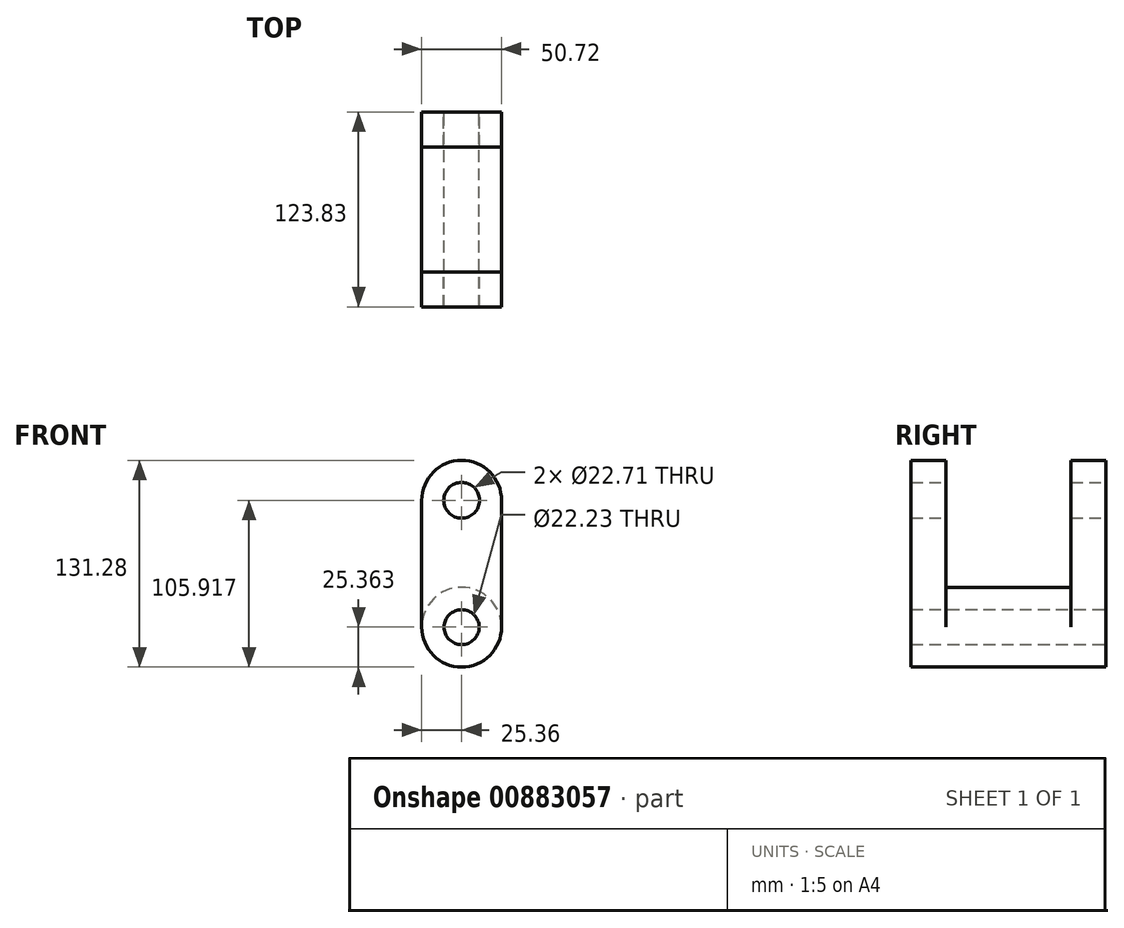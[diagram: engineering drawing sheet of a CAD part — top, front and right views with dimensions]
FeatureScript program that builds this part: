
annotation { "Feature Type Name" : "Feature", "Feature Type Description" : "" }
export const myFeature = defineFeature(function(context is Context, id is Id, definition is map)
    precondition{}
    {
        {
            var Q0;
            Q0=qCreatedBy(makeId("Front.planeOp"),FACE);
            var sketch = newSketch(context, id + "F0", { "sketchPlane" : qUnion([Q0])});
            skLineSegment(sketch, "E0.left", {"start": v(25.36, 40.28) * mm, "end": v(25.36, -40.28) * mm});
            skLineSegment(sketch, "E0.right", {"start": v(-25.36, 40.28) * mm, "end": v(-25.36, -40.28) * mm});
            skPoint(sketch, "E0.middle", {"position": v(0, 0) * mm});
            skArc(sketch, "E1", {"start": v(25.36, 40.28) * mm, "mid": v(0, 65.64) * mm, "end": v(-25.36, 40.28) * mm});
            skArc(sketch, "E2", {"start": v(-25.36, -40.28) * mm, "mid": v(0, -65.64) * mm, "end": v(25.36, -40.28) * mm});
            skCircle(sketch, "E3", {"center": v(0, 40.28) * mm, "radius": 11.35 * mm});
            skSolve(sketch);
        }
        {
            var Q0;
            Q0=makeQuery(id+"F0.imprint","IMPRINT",FACE,{"disambiguationData":[TD([[makeQuery(id+"F0.imprint","IMPRINT",EDGE,{"derivedFrom":sQuery(id+"F0.wireOp",EDGE,"E0.left")}),-1.0]])]});
            extrude(context, id + "F1", {"entities" : qUnion([Q0]), "depth" : 22.22 * mm, "offsetDistance" : 25.4 * mm});
        }
        {
            var Q0;
            Q0=makeQuery(id+"F1.opExtrude","SWEPT_BODY",BODY,{"disambiguationData":[OSD([sQuery(id+"F0.wireOp",EDGE,"E0.left"),sQuery(id+"F0.wireOp",EDGE,"E0.right"),sQuery(id+"F0.wireOp",EDGE,"E1"),sQuery(id+"F0.wireOp",EDGE,"E2"),sQuery(id+"F0.wireOp",EDGE,"E3")])]});
            transform(context, id + "F2", {"entities" : qUnion([Q0]), "transformType" : TransformType.TRANSLATION_3D, "dx" : 0 * mm, "dy" : 101.6 * mm, "dz" : 0 * mm, "makeCopy" : true});
        }
        {
            var Q0;
            Q0=makeQuery(id+"F1.opExtrude","CAP_FACE",FACE,{"disambiguationData":[OSD([sQuery(id+"F0.wireOp",EDGE,"E0.left"),sQuery(id+"F0.wireOp",EDGE,"E0.right"),sQuery(id+"F0.wireOp",EDGE,"E1"),sQuery(id+"F0.wireOp",EDGE,"E2"),sQuery(id+"F0.wireOp",EDGE,"E3")])],"isStart":true});
            var sketch = newSketch(context, id + "F3", { "sketchPlane" : qUnion([Q0])});
            skCircle(sketch, "E4", {"center": v(0, -40.28) * mm, "radius": 25.36 * mm});
            skSolve(sketch);
        }
        {
            var Q0;
            {var subQ0=sQuery(id+"F3.wireOp",EDGE,"E4");Q0=makeQuery(id+"F3.imprint","IMPRINT",FACE,{"disambiguationData":[TD([[makeQuery(id+"F3.imprint","IMPRINT",EDGE,{"disambiguationData":[OD(0.0)],"derivedFrom":subQ0}),1.0]])]});}
            var Q1;
            Q1=makeQuery(id+"F2.opPattern","COPY",FACE,{"derivedFrom":makeQuery(id+"F1.opExtrude","CAP_FACE",FACE,{"disambiguationData":[OSD([sQuery(id+"F0.wireOp",EDGE,"E0.left"),sQuery(id+"F0.wireOp",EDGE,"E0.right"),sQuery(id+"F0.wireOp",EDGE,"E1"),sQuery(id+"F0.wireOp",EDGE,"E2"),sQuery(id+"F0.wireOp",EDGE,"E3")])],"isStart":false}),"instanceName":"1"});
            var Q2;
            Q2=makeQuery(id+"F2.opPattern","COPY",FACE,{"derivedFrom":makeQuery(id+"F1.opExtrude","CAP_FACE",FACE,{"disambiguationData":[OSD([sQuery(id+"F0.wireOp",EDGE,"E0.left"),sQuery(id+"F0.wireOp",EDGE,"E0.right"),sQuery(id+"F0.wireOp",EDGE,"E1"),sQuery(id+"F0.wireOp",EDGE,"E2"),sQuery(id+"F0.wireOp",EDGE,"E3")])],"isStart":false}),"instanceName":"1"});
            extrude(context, id + "F4", {"entities" : qUnion([Q0]), "operationType" : NewBodyOperationType.ADD, "endBound" : BoundingType.UP_TO_SURFACE, "depth" : 25.4 * mm, "endBoundEntityFace" : qUnion([Q1]), "offsetDistance" : 25.4 * mm});
        }
        {
            var Q0;
            Q0=makeQuery(id+"F2.opPattern","COPY",FACE,{"derivedFrom":makeQuery(id+"F1.opExtrude","CAP_FACE",FACE,{"disambiguationData":[OSD([sQuery(id+"F0.wireOp",EDGE,"E0.left"),sQuery(id+"F0.wireOp",EDGE,"E0.right"),sQuery(id+"F0.wireOp",EDGE,"E1"),sQuery(id+"F0.wireOp",EDGE,"E2"),sQuery(id+"F0.wireOp",EDGE,"E3")])],"isStart":true}),"instanceName":"1"});
            var sketch = newSketch(context, id + "F5", { "sketchPlane" : qUnion([Q0])});
            skPoint(sketch, "E5", {"position": v(0, -40.28) * mm});
            skSolve(sketch);
        }
        {
            var Q0;
            Q0=sQuery(id+"F5.wireOp",VERTEX,"E5");
            var Q1;
            Q1=makeQuery(id+"F1.opExtrude","SWEPT_BODY",BODY,{"disambiguationData":[OSD([sQuery(id+"F0.wireOp",EDGE,"E0.left"),sQuery(id+"F0.wireOp",EDGE,"E0.right"),sQuery(id+"F0.wireOp",EDGE,"E1"),sQuery(id+"F0.wireOp",EDGE,"E2"),sQuery(id+"F0.wireOp",EDGE,"E3")])]});
            hole(context, id + "F6", {"style" : HoleStyle.SIMPLE, "endStyle" : HoleEndStyle.THROUGH, "holeDiameter" : 22.22 * mm, "majorDiameter" : 6.35 * mm, "isTappedThrough" : true, "tappedDepth" : 12.7 * mm, "tapClearance" : 3, "locations" : qUnion([Q0]), "scope" : qUnion([Q1])});
        }
    });
